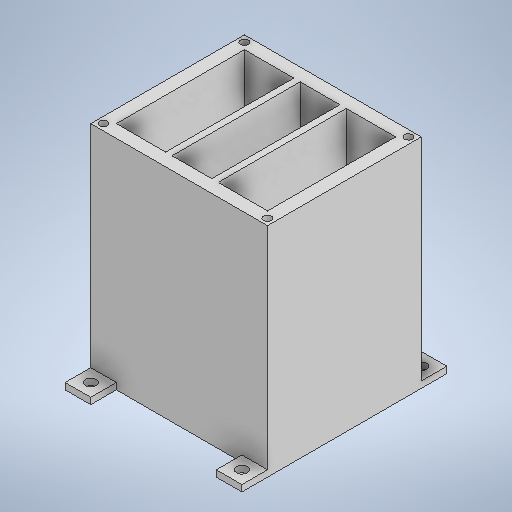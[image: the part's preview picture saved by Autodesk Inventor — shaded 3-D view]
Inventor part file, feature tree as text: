
AUTODESK INVENTOR PART (.ipt)
format: ipt  version: 2025 (Build 290162000, 162)  size: 321,536 bytes
history: native  units: mm
features: sketch x9, extrude x8, plane x2, mirror x2
ambient origin geometry x8: Origin, YZ Plane, XZ Plane, XY Plane, X Axis, Y Axis, Z Axis, Center Point
bodies: Solid1 (feature_tree)
feature tree (21):
  sketch  "Sketch1"  dims[d0=69.0mm d1=60.0mm]
  extrude  "Extrusion1"  Depth=60.0mm
  extrude  "Extrusion2"  TaperAngle=0.0deg  [1 undecoded]
  extrude  "Extrusion3"  Depth=50.0mm
  extrude  "Extrusion4"  TaperAngle=0.0deg  [1 undecoded]
  extrude  "Extrusion5"  Depth=2.5mm
  plane  "Work Plane2"
  mirror  "Mirror2"
  extrude  "Extrusion6"  Depth=2.5mm
  extrude  "Extrusion7"  Depth=10.0mm TaperAngle=0.0deg
  plane  "Work Plane3"
  mirror  "Mirror3"
  extrude  "Extrusion8"  Depth=2.5mm
  sketch  "Sketch2"  dims[d2=85.0mm d3=0.0mm]
  sketch  "Sketch3"  dims[d4=59.0mm d5=50.0mm]
  sketch  "Sketch4"  dims[d6=80.0mm d7=0.0mm]
  sketch  "Sketch5"  dims[d8=3.1mm d9=2.5mm]
  sketch  "Sketch6"  dims[d10=2.5mm d11=2.5mm]
  sketch  "Sketch7"  dims[d12=2.5mm d13=10.0mm d14=0.0mm]
  sketch  "Sketch8"  dims[d15=10.0mm d16=2.5mm]
  sketch  "Sketch9"  dims[d17=10.0mm d18=0.0mm d19=4.2mm d20=5.0mm d21=5.0mm d22=0.0mm d23=0.0mm d24=30.0mm d25=10.0mm d26=0.0mm d27=13.0mm d28=5.0mm d29=5.0mm d30=1.25mm d31=1.25mm d32=80.0mm d33=0.0mm d34=5.0mm d35=0.0mm]
note: 2 required parameter values undecoded (feature->parameter linkage not recoverable at this tier; creation-order binding heuristic only, values carry confidence <= 0.55)
